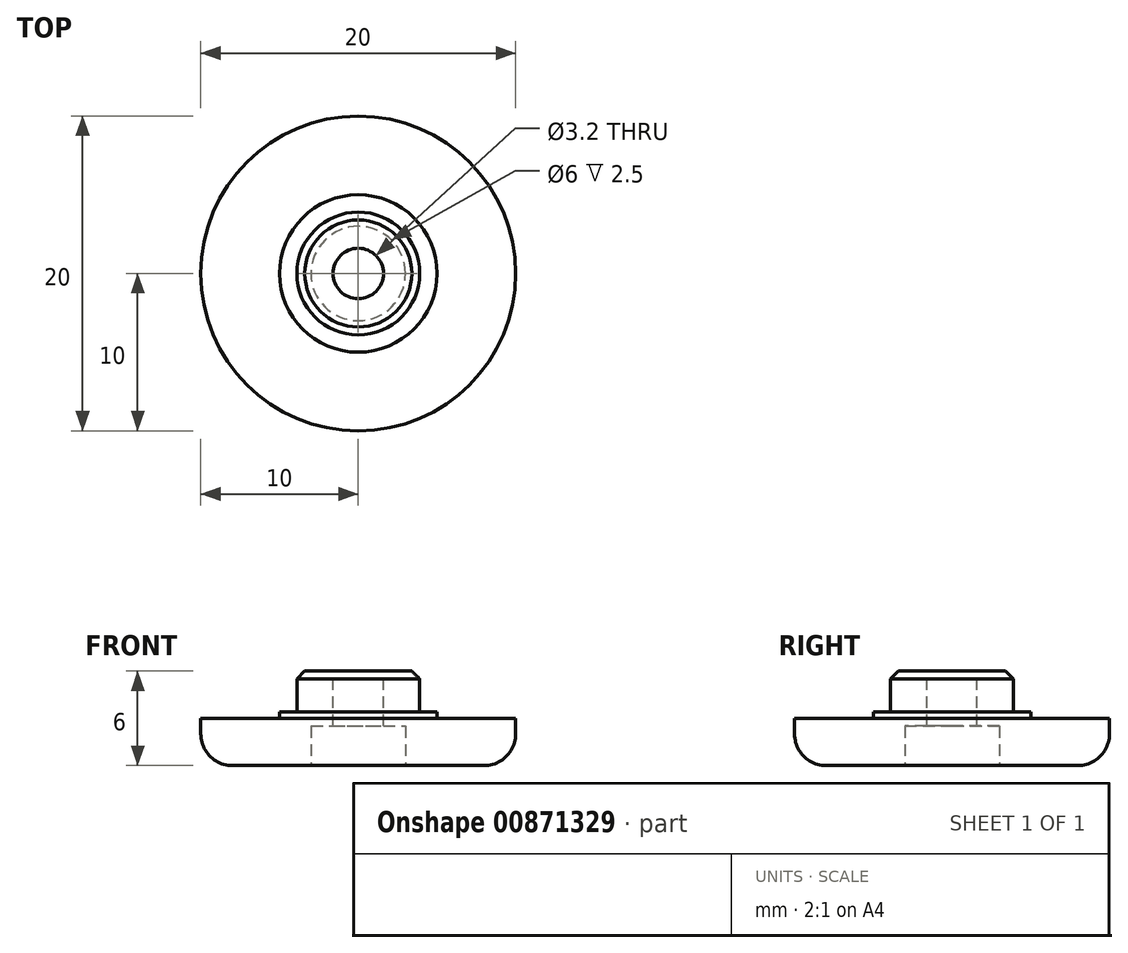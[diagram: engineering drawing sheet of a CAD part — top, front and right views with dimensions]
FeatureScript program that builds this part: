
annotation { "Feature Type Name" : "Feature", "Feature Type Description" : "" }
export const myFeature = defineFeature(function(context is Context, id is Id, definition is map)
    precondition{}
    {
        {
            var Q0;
            Q0=qCreatedBy(makeId("Front.planeOp"),FACE);
            var sketch = newSketch(context, id + "F0", { "sketchPlane" : qUnion([Q0])});
            skLineSegment(sketch, "E0", {"start": v(0, 6) * mm, "end": v(3.9, 6) * mm});
            skLineSegment(sketch, "E1", {"start": v(3.9, 6) * mm, "end": v(3.9, 3) * mm});
            skLineSegment(sketch, "E2", {"start": v(3.9, 3) * mm, "end": v(10, 3) * mm});
            skLineSegment(sketch, "E3", {"start": v(10, 3) * mm, "end": v(10, 0) * mm});
            skLineSegment(sketch, "E4", {"start": v(10, 0) * mm, "end": v(0, 0) * mm});
            skLineSegment(sketch, "E5", {"start": v(0, 6) * mm, "end": v(0, 0) * mm});
            skSolve(sketch);
        }
        {
            var Q0;
            Q0=makeQuery(id+"F0.imprint","IMPRINT",FACE,{"disambiguationData":[TD([[makeQuery(id+"F0.imprint","IMPRINT",EDGE,{"derivedFrom":sQuery(id+"F0.wireOp",EDGE,"E0")}),-1.0]])]});
            var Q1;
            Q1=sQuery(id+"F0.wireOp",EDGE,"E5");
            revolve(context, id + "F1", {"surfaceOperationType" : NewSurfaceOperationType.NEW, "entities" : qUnion([Q0]), "axis" : qUnion([Q1]), "revolveType" : RevolveType.FULL});
        }
        {
            var Q0;
            Q0=makeQuery(id+"F1.opRevolve","SWEPT_EDGE",EDGE,{"disambiguationData":[OSD([sQuery(id+"F0.wireOp",EDGE,"E0"),sQuery(id+"F0.wireOp",EDGE,"E1")])]});
            chamfer(context, id + "F2", {"entities" : qUnion([Q0]), "width" : 0.5 * mm, "tangentPropagation" : true});
        }
        {
            var Q0;
            Q0=makeQuery(id+"F1.opRevolve","SWEPT_FACE",FACE,{"disambiguationData":[OSD([sQuery(id+"F0.wireOp",EDGE,"E2")])]});
            var sketch = newSketch(context, id + "F3", { "sketchPlane" : qUnion([Q0])});
            skCircle(sketch, "E6", {"center": v(0, 0) * mm, "radius": 5 * mm});
            skSolve(sketch);
        }
        {
            var Q0;
            Q0=makeQuery(id+"F3.imprint","IMPRINT",FACE,{"disambiguationData":[TD([[makeQuery(id+"F3.imprint","IMPRINT",EDGE,{"derivedFrom":sQuery(id+"F3.wireOp",EDGE,"E6")}),1.0]])]});
            extrude(context, id + "F4", {"entities" : qUnion([Q0]), "operationType" : NewBodyOperationType.ADD, "depth" : 0.4 * mm, "offsetDistance" : 25 * mm});
        }
        {
            var Q0;
            Q0=makeQuery(id+"F1.opRevolve","SWEPT_EDGE",EDGE,{"disambiguationData":[OSD([sQuery(id+"F0.wireOp",EDGE,"E3"),sQuery(id+"F0.wireOp",EDGE,"E4")])]});
            fillet(context, id + "F5", {"entities" : qUnion([Q0]), "radius" : 2 * mm, "tangentPropagation" : true, "allowEdgeOverflow" : false});
        }
        {
            var Q0;
            Q0=makeQuery(id+"F1.opRevolve","SWEPT_FACE",FACE,{"disambiguationData":[OSD([sQuery(id+"F0.wireOp",EDGE,"E0")])]});
            var sketch = newSketch(context, id + "F6", { "sketchPlane" : qUnion([Q0])});
            skCircle(sketch, "E7", {"center": v(0, 0) * mm, "radius": 1.6 * mm});
            skSolve(sketch);
        }
        {
            var Q0;
            Q0=makeQuery(id+"F6.imprint","IMPRINT",FACE,{"disambiguationData":[TD([[makeQuery(id+"F6.imprint","IMPRINT",EDGE,{"derivedFrom":sQuery(id+"F6.wireOp",EDGE,"E7")}),1.0]])]});
            extrude(context, id + "F7", {"entities" : qUnion([Q0]), "operationType" : NewBodyOperationType.REMOVE, "oppositeDirection" : true, "depth" : 25 * mm, "offsetDistance" : 25 * mm});
        }
        {
            var Q0;
            Q0=makeQuery(id+"F1.opRevolve","SWEPT_FACE",FACE,{"disambiguationData":[OSD([sQuery(id+"F0.wireOp",EDGE,"E4")])]});
            var sketch = newSketch(context, id + "F8", { "sketchPlane" : qUnion([Q0])});
            skCircle(sketch, "E8", {"center": v(0, 0) * mm, "radius": 3 * mm});
            skSolve(sketch);
        }
        {
            var Q0;
            Q0=makeQuery(id+"F8.imprint","IMPRINT",FACE,{"disambiguationData":[TD([[makeQuery(id+"F8.imprint","IMPRINT",EDGE,{"derivedFrom":sQuery(id+"F8.wireOp",EDGE,"bd10d42b-fc38-4f4a-b552-ecd5d630514c.0")}),-1.0]])]});
            var Q1;
            Q1=makeQuery(id+"F8.imprint","IMPRINT",FACE,{"disambiguationData":[TD([[makeQuery(id+"F8.imprint","IMPRINT",EDGE,{"derivedFrom":sQuery(id+"F8.wireOp",EDGE,"E8")}),1.0]])]});
            extrude(context, id + "F9", {"entities" : qUnion([Q0, Q1]), "operationType" : NewBodyOperationType.REMOVE, "oppositeDirection" : true, "depth" : 2.5 * mm, "offsetDistance" : 25 * mm});
        }
    });
